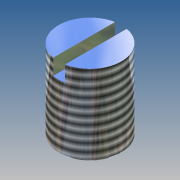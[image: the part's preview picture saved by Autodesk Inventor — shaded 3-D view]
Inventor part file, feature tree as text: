
AUTODESK INVENTOR PART (.ipt)
format: ipt  version: 2012 (Build 160160000, 160)  size: 113,664 bytes
history: native  units: mm (DEFAULTED — no unit token found)
features: extrude x2, sketch x2, chamfer x1, thread x1
ambient origin geometry x8: Origin, YZ Plane, XZ Plane, XY Plane, X Axis, Y Axis, Z Axis, Center Point
bodies: Solid1 (feature_tree)
feature tree (6):
  extrude  "Extrusion1"  Depth=10.3mm TaperAngle=0.0deg
  chamfer  "Chamfer1"  Distance=0.3mm
  thread  "Thread1"  [1 undecoded]
  extrude  "Extrusion2"  Depth=0.75mm
  sketch  "Sketch1"  dims[d0=8.0mm d1=10.3mm d2=0.0mm d3=0.3mm d4=0.3mm d5=10.0mm d6=0.0mm]
  sketch  "Sketch2"  dims[d7=1.5mm d8=0.75mm d9=2.0mm d10=0.0mm d11=45.0deg]
note: 1 required parameter value undecoded (feature->parameter linkage not recoverable at this tier; creation-order binding heuristic only, values carry confidence <= 0.55)
